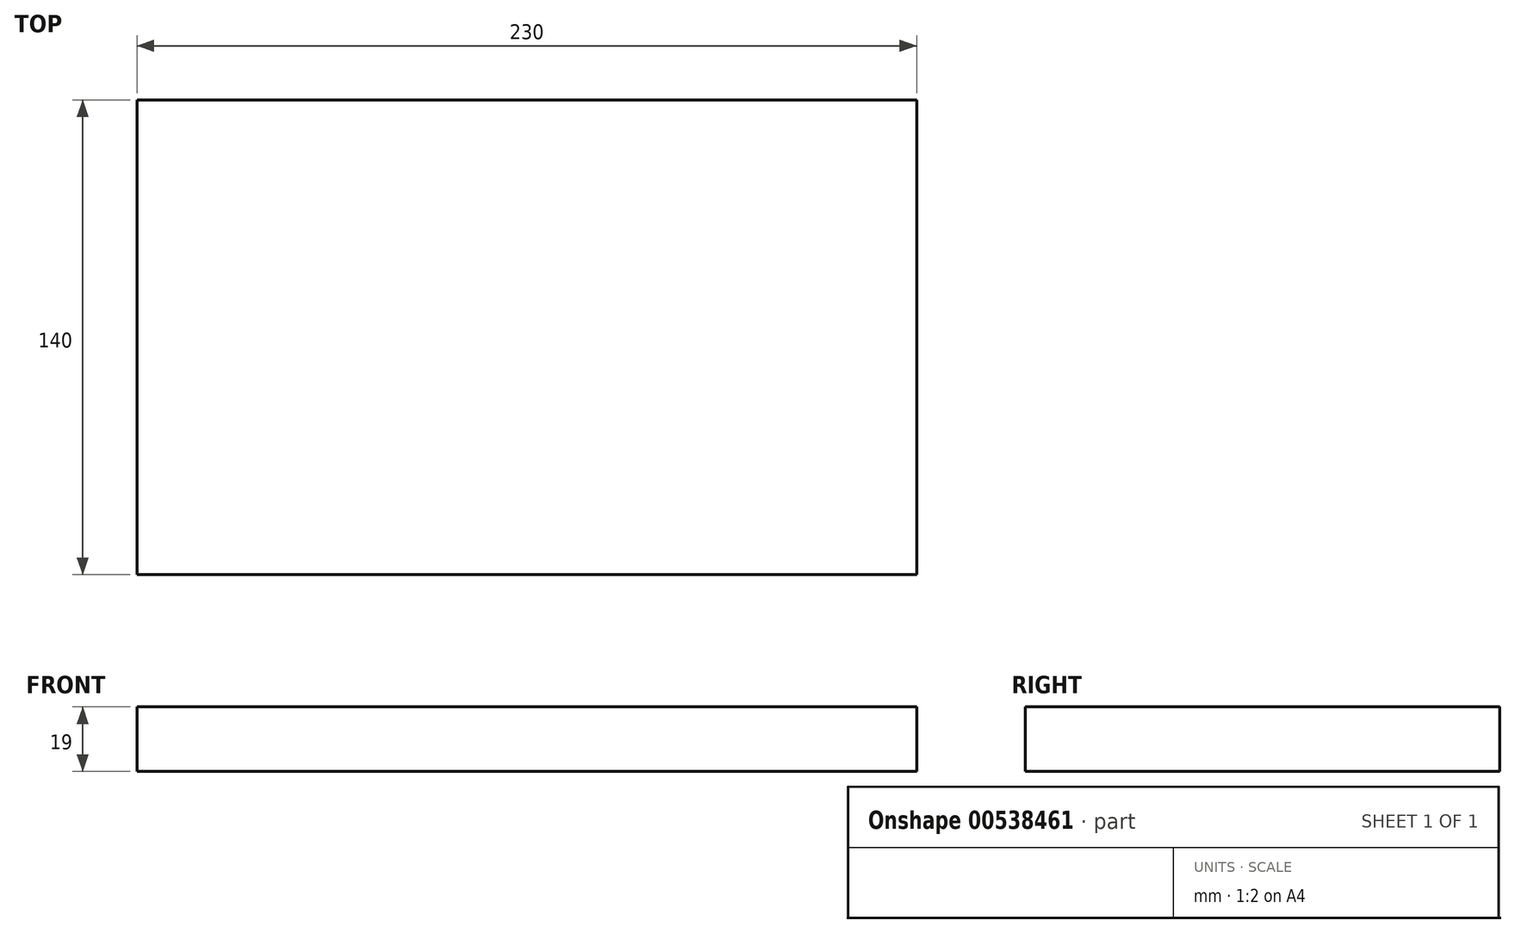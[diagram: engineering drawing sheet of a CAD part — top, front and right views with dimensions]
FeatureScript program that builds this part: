
annotation { "Feature Type Name" : "Feature", "Feature Type Description" : "" }
export const myFeature = defineFeature(function(context is Context, id is Id, definition is map)
    precondition{}
    {
        {
            var Q0;
            Q0=qCreatedBy(makeId("Top.planeOp"),FACE);
            var sketch = newSketch(context, id + "F0", { "sketchPlane" : qUnion([Q0])});
            skLineSegment(sketch, "E0.bottom", {"start": v(-115, 70) * mm, "end": v(115, 70) * mm});
            skLineSegment(sketch, "E0.top", {"start": v(-115, -70) * mm, "end": v(115, -70) * mm});
            skLineSegment(sketch, "E0.left", {"start": v(-115, 70) * mm, "end": v(-115, -70) * mm});
            skLineSegment(sketch, "E0.right", {"start": v(115, 70) * mm, "end": v(115, -70) * mm});
            skPoint(sketch, "E0.middle", {"position": v(0, 0) * mm});
            skSolve(sketch);
        }
        {
            var Q0;
            Q0=makeQuery(id+"F0.imprint","IMPRINT",FACE,{"disambiguationData":[TD([[makeQuery(id+"F0.imprint","IMPRINT",EDGE,{"derivedFrom":sQuery(id+"F0.wireOp",EDGE,"E0.bottom")}),-1.0]])]});
            extrude(context, id + "F1", {"entities" : qUnion([Q0]), "depth" : 19 * mm, "offsetDistance" : 25 * mm});
        }
    });
